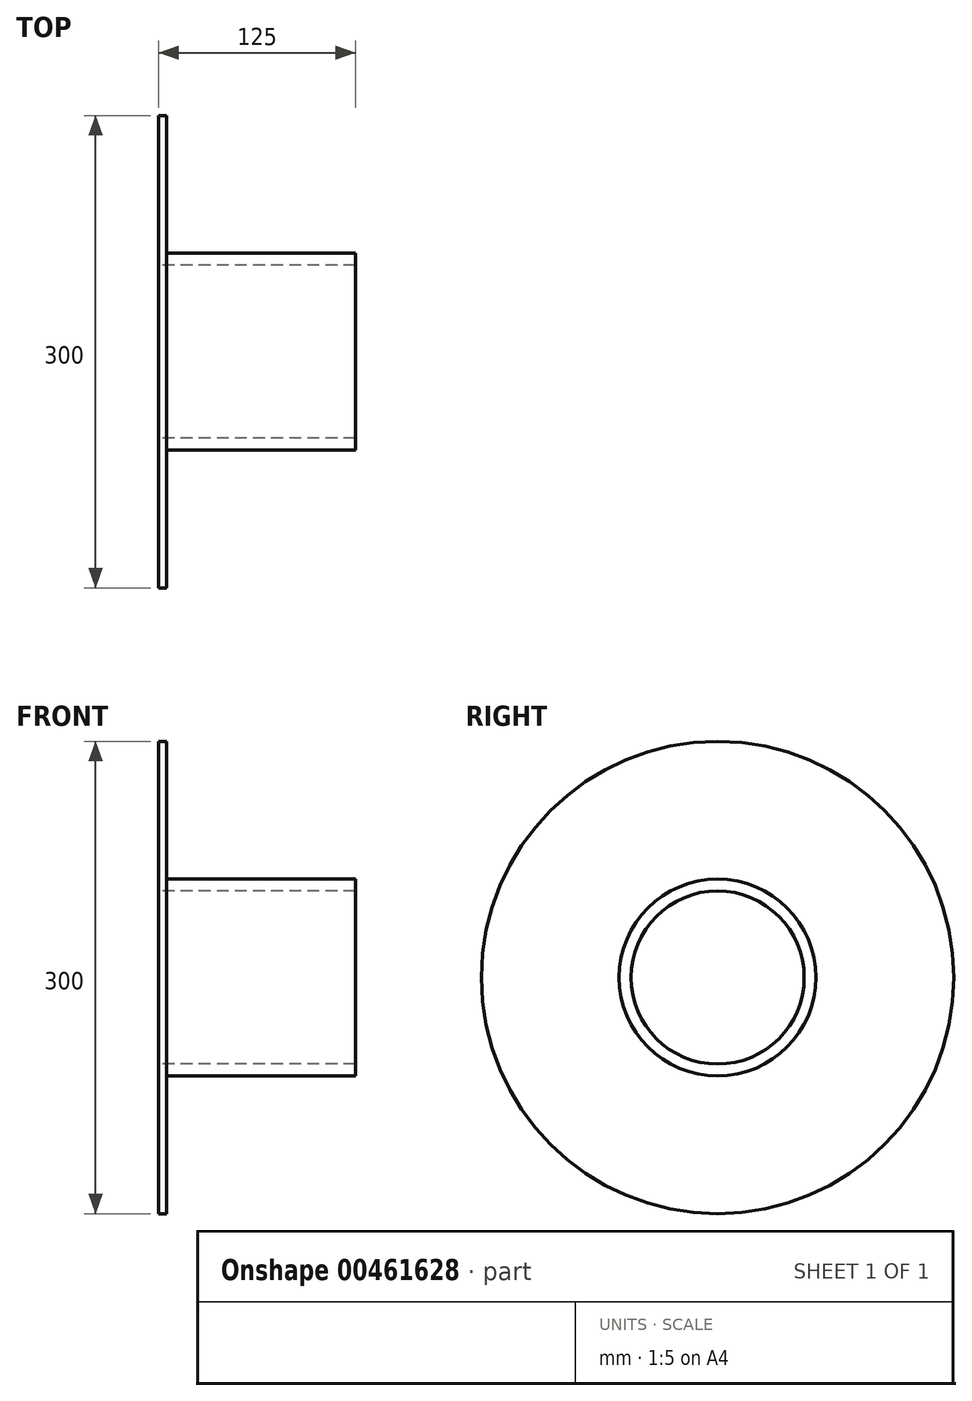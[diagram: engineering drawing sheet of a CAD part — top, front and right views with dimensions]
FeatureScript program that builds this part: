
annotation { "Feature Type Name" : "Feature", "Feature Type Description" : "" }
export const myFeature = defineFeature(function(context is Context, id is Id, definition is map)
    precondition{}
    {
        {
            var Q0;
            Q0=qCreatedBy(makeId("Front.planeOp"),FACE);
            var sketch = newSketch(context, id + "F0", { "sketchPlane" : qUnion([Q0])});
            skLineSegment(sketch, "E0.bottom", {"start": v(0, 150) * mm, "end": v(5, 150) * mm});
            skLineSegment(sketch, "E0.top", {"start": v(0, 55) * mm, "end": v(5, 55) * mm});
            skLineSegment(sketch, "E0.left", {"start": v(0, 150) * mm, "end": v(0, 55) * mm});
            skLineSegment(sketch, "E0.right", {"start": v(5, 150) * mm, "end": v(5, 55) * mm});
            skLineSegment(sketch, "E1.bottom", {"start": v(5, 62.5) * mm, "end": v(125, 62.5) * mm});
            skLineSegment(sketch, "E1.top", {"start": v(5, 55) * mm, "end": v(125, 55) * mm});
            skLineSegment(sketch, "E1.left", {"start": v(5, 62.5) * mm, "end": v(5, 55) * mm});
            skLineSegment(sketch, "E1.right", {"start": v(125, 62.5) * mm, "end": v(125, 55) * mm});
            skLineSegment(sketch, "E2", {"start": v(0, 0) * mm, "end": v(76.91, 0) * mm, "construction": true});
            skSolve(sketch);
        }
        {
            var Q0;
            Q0=makeQuery(id+"F0.imprint","IMPRINT",FACE,{"disambiguationData":[TD([[makeQuery(id+"F0.imprint","IMPRINT",EDGE,{"derivedFrom":sQuery(id+"F0.wireOp",EDGE,"E0.bottom")}),-1.0]])]});
            var Q1;
            Q1=makeQuery(id+"F0.imprint","IMPRINT",FACE,{"disambiguationData":[TD([[makeQuery(id+"F0.imprint","IMPRINT",EDGE,{"derivedFrom":sQuery(id+"F0.wireOp",EDGE,"E1.bottom")}),-1.0]])]});
            var Q2;
            Q2=sQuery(id+"F0.wireOp",EDGE,"E2");
            revolve(context, id + "F1", {"entities" : qUnion([Q0, Q1]), "axis" : qUnion([Q2]), "revolveType" : RevolveType.FULL});
        }
        {
            var Q0;
            Q0=makeQuery(id+"F1.opRevolve","SWEPT_FACE",FACE,{"disambiguationData":[OSD([sQuery(id+"F0.wireOp",EDGE,"E0.right")])]});
            var sketch = newSketch(context, id + "F2", { "sketchPlane" : qUnion([Q0])});
            skCircle(sketch, "E3", {"center": v(-120, 0) * mm, "radius": 8.5 * mm});
            skCircle(sketch, "E4.1.0", {"center": v(0, -120) * mm, "radius": 8.5 * mm});
            skCircle(sketch, "E4.2.0", {"center": v(120, 0) * mm, "radius": 8.5 * mm});
            skCircle(sketch, "E4.3.0", {"center": v(0, 120) * mm, "radius": 8.5 * mm});
            skPoint(sketch, "E4.center", {"position": v(0, 0) * mm});
            skSolve(sketch);
        }
        {
            var Q0;
            Q0=makeQuery(id+"F2.imprint","IMPRINT",FACE,{"disambiguationData":[TD([[makeQuery(id+"F2.imprint","IMPRINT",EDGE,{"derivedFrom":sQuery(id+"F2.wireOp",EDGE,"E3")}),1.0]])]});
            extrude(context, id + "F3", {"entities" : qUnion([Q0]), "operationType" : NewBodyOperationType.ADD, "endBound" : BoundingType.UP_TO_NEXT, "oppositeDirection" : true, "depth" : 5 * mm});
        }
    });
